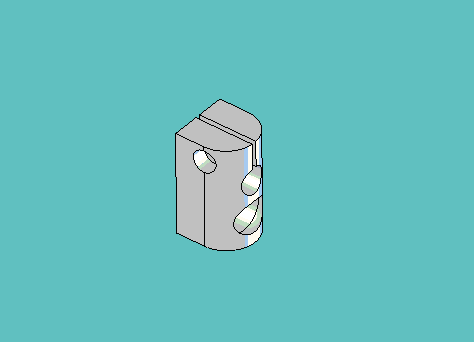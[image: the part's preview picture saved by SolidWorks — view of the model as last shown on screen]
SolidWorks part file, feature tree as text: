
SOLIDWORKS PART (.sldprt)
format: sldprt  version: not decoded by parser v0  size: 730,624 bytes
history: native  units: mm
features: sketch x10, cut_extrude x7, extrude x2, material x1, revolve x1, boolean_combine x1, plane x1, fillet x1 (+11 scaffold rows collapsed)
feature tree (35):
  scaffold x11  (default folders/planes/origin — collapsed)
  material  "Material <not specified>"
  sketch  "Sketch1"  dims[D1=19.05mm]
  extrude  "Extrude1"  Depth=33.3375mm
  sketch  "Sketch2"  dims[c1.D1=3.4544mm c1.D2=2.159mm c1.D6=2.159mm c1.D7=3.4544mm c1.D3=8.7376mm c1.D4=28.3464mm c2.D3=8.7376mm c2.D4=28.3464mm c2.D5=8.7376mm c2.D8=28.3464mm]
  cut_extrude  "Cut-Extrude1"  [1 undecoded]
  sketch  "Sketch3"  dims[D4=12.7mm D1=8.7376mm D2=12.7mm D3=6.35mm D5=7.62mm D6=5.1562mm]
  revolve  "Revolve1"  Angle=360deg
  boolean_combine  "Combine1"
  sketch  "Sketch4"  dims[D1=8.5852mm D2=20.6502mm]
  cut_extrude  "Cut-Extrude2"  [1 undecoded]
  sketch  "Sketch5"  dims[D1=4.3688mm]
  cut_extrude  "Cut-Extrude3"  [1 undecoded]
  plane  "Plane1"  Offset=12.7mm
  sketch  "Sketch6"  dims[D1=~7.14375mm]
  cut_extrude  "Cut-Extrude4"  Depth=7.9375mm
  sketch  "Sketch7"  dims[D1=~0.79375mm D2=~0.79375mm]
  cut_extrude  "Cut-Extrude5"  Depth=12.7mm
  sketch  "Sketch11"  dims[D1=17.272mm D2=17.272mm D3=16.002mm]
  extrude  "Extrude2"  Depth=4.7625mm
  fillet  "Fillet1"  Radius=3.175mm
  sketch  "Sketch8"  dims[D1=4.064mm D2=4.064mm D3=13.589mm D4=13.589mm D5=3.175mm D6=3.175mm]
  cut_extrude  "Cut-Extrude6"  Depth=4.7625mm
  sketch  "Sketch10"  dims[D1=2.159mm]
  cut_extrude  "Cut-Extrude7"  [1 undecoded]
decode coverage: 17 of 22 modeling features carry decoded parameters
note: ~ marks probable driven/reference dimensions
note: 4 parameter values undecoded
summary: no parameter record found for 4 features
note: suppression state not decoded; provenance and decode notes live in map.json
